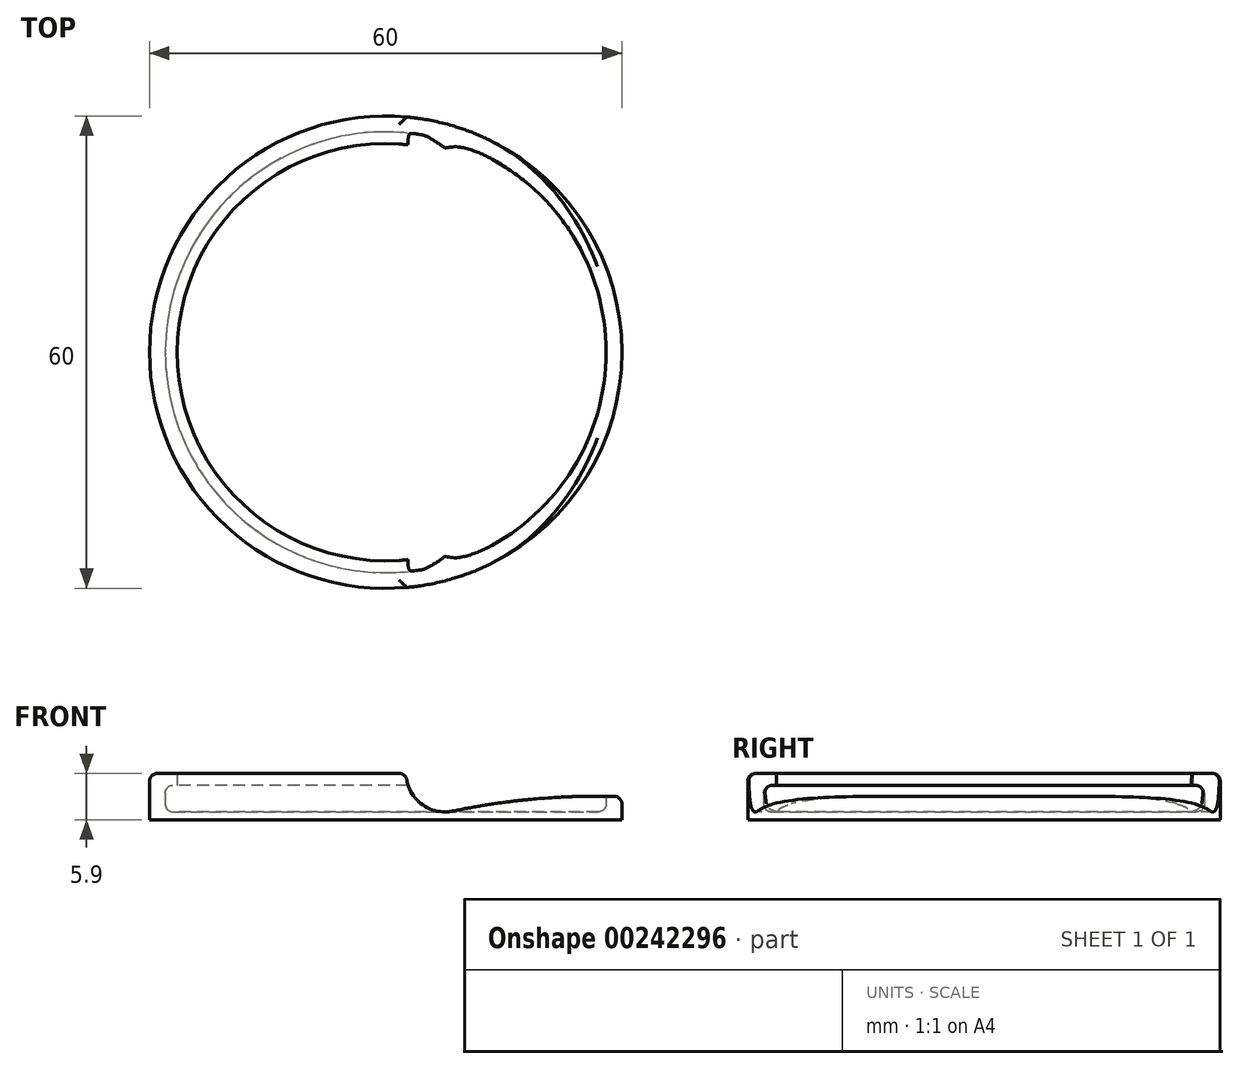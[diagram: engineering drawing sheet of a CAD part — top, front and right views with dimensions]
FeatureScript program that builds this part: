
annotation { "Feature Type Name" : "Feature", "Feature Type Description" : "" }
export const myFeature = defineFeature(function(context is Context, id is Id, definition is map)
    precondition{}
    {
        {
            var Q0;
            Q0=qCreatedBy(makeId("Front.planeOp"),FACE);
            var sketch = newSketch(context, id + "F0", { "sketchPlane" : qUnion([Q0])});
            skLineSegment(sketch, "E0", {"start": v(0, 0) * mm, "end": v(-27, 0) * mm});
            skLineSegment(sketch, "E1", {"start": v(-28, 1) * mm, "end": v(-28, 2.4) * mm});
            skLineSegment(sketch, "E2", {"start": v(-27, 3.4) * mm, "end": v(-26.5, 3.4) * mm});
            skLineSegment(sketch, "E3", {"start": v(-26.5, 3.4) * mm, "end": v(-26.5, 4.9) * mm});
            skLineSegment(sketch, "E4", {"start": v(-26.5, 4.9) * mm, "end": v(-29, 4.9) * mm});
            skLineSegment(sketch, "E5", {"start": v(-30, 3.9) * mm, "end": v(-30, -1) * mm});
            skLineSegment(sketch, "E6", {"start": v(0, -1) * mm, "end": v(0, 0) * mm});
            skPoint(sketch, "E7.visualSharp", {"position": v(-30, 4.9) * mm});
            skArc(sketch, "E7.filletArc", {"start": v(-29, 4.9) * mm, "mid": v(-29.7, 4.6) * mm, "end": v(-30, 3.9) * mm});
            skPoint(sketch, "E8.visualSharp", {"position": v(-28, 3.4) * mm});
            skArc(sketch, "E8.filletArc", {"start": v(-27, 3.4) * mm, "mid": v(-27.7, 3.1) * mm, "end": v(-28, 2.4) * mm});
            skPoint(sketch, "E9.visualSharp", {"position": v(-28, 0) * mm});
            skArc(sketch, "E9.filletArc", {"start": v(-28, 1) * mm, "mid": v(-27.7, 0.3) * mm, "end": v(-27, 0) * mm});
            skLineSegment(sketch, "E10", {"start": v(0, 0) * mm, "end": v(0, 0.5) * mm});
            skLineSegment(sketch, "E11", {"start": v(-28, 2) * mm, "end": v(-29, 2) * mm});
            skArc(sketch, "E12", {"start": v(-30, 1) * mm, "mid": v(-29.7, 1.7) * mm, "end": v(-29, 2) * mm});
            skLineSegment(sketch, "E13", {"start": v(0, -1) * mm, "end": v(-30, -1) * mm});
            skPoint(sketch, "E14.orphan", {"position": v(0, -2) * mm});
            skSolve(sketch);
        }
        {
            var Q0;
            Q0=makeQuery(id+"F0.imprint","IMPRINT",FACE,{"disambiguationData":[TD([[makeQuery(id+"F0.imprint","IMPRINT",EDGE,{"derivedFrom":sQuery(id+"F0.wireOp",EDGE,"E0")}),1.0]])]});
            var Q1;
            Q1=sQuery(id+"F0.wireOp",EDGE,"E6");
            revolve(context, id + "F1", {"entities" : qUnion([Q0]), "axis" : qUnion([Q1]), "revolveType" : RevolveType.FULL});
        }
        {
            var Q0;
            Q0=makeQuery(id+"F0.imprint","IMPRINT",FACE,{"disambiguationData":[TD([[makeQuery(id+"F0.imprint","IMPRINT",EDGE,{"derivedFrom":sQuery(id+"F0.wireOp",EDGE,"E2")}),1.0]])]});
            var Q1;
            Q1=sQuery(id+"F0.wireOp",EDGE,"E6");
            revolve(context, id + "F2", {"operationType" : NewBodyOperationType.ADD, "entities" : qUnion([Q0]), "axis" : qUnion([Q1]), "revolveType" : RevolveType.SYMMETRIC, "angle" : 210 * degree});
        }
        {
            var Q0;
            Q0=qCreatedBy(makeId("Front.planeOp"),FACE);
            var sketch = newSketch(context, id + "F3", { "sketchPlane" : qUnion([Q0])});
            skLineSegment(sketch, "E15.0", {"start": v(7.5, 4.9) * mm, "end": v(-29, 4.9) * mm});
            skLineSegment(sketch, "E16.0", {"start": v(7.5, 2) * mm, "end": v(29, 2) * mm});
            skCircle(sketch, "E17", {"center": v(7.5, 4.9) * mm, "radius": 4.9 * mm});
            skArc(sketch, "E18", {"start": v(2.68, 4.07) * mm, "mid": v(2.34, 4.66) * mm, "end": v(1.7, 4.9) * mm});
            skArc(sketch, "E19", {"start": v(26.89, 2) * mm, "mid": v(17.65, 1.52) * mm, "end": v(8.5, 0.1) * mm});
            skLineSegment(sketch, "E20.0.0", {"start": v(-27, 0) * mm, "end": v(27, 0) * mm});
            skSolve(sketch);
        }
        {
            var Q0;
            {var subQ0=sQuery(id+"F3.wireOp",EDGE,"E18");Q0=makeQuery(id+"F3.imprint","IMPRINT",FACE,{"disambiguationData":[TD([[makeQuery(id+"F3.imprint","IMPRINT",EDGE,{"derivedFrom":subQ0}),-1.0]])]});}
            var Q1;
            {var subQ0=sQuery(id+"F3.wireOp",EDGE,"E17");var subQ4=makeQuery(id+"F3.imprint","INTERSECT",VERTEX,{"derivedFrom":[subQ0,sQuery(id+"F3.wireOp",EDGE,"P1Wmpzot-LLGH-U3KA-p0y4-jWoeoiDEk2Na")]});Q1=makeQuery(id+"F3.imprint","IMPRINT",FACE,{"disambiguationData":[TD([[makeQuery(id+"F3.imprint","IMPRINT",EDGE,{"disambiguationData":[TD([[subQ4,1.0]])],"derivedFrom":subQ0}),1.0]])]});}
            var Q2;
            {var subQ0=sQuery(id+"F3.wireOp",EDGE,"E19");var subQ5=sQuery(id+"F3.wireOp",EDGE,"45842464-4a71-46be-bf13-90a27824be04.0");var subQ6=makeQuery(id+"F3.imprint","INTERSECT",VERTEX,{"derivedFrom":[subQ5,subQ0]});Q2=makeQuery(id+"F3.imprint","IMPRINT",FACE,{"disambiguationData":[TD([[makeQuery(id+"F3.imprint","IMPRINT",EDGE,{"disambiguationData":[TD([[subQ6,1.0]])],"derivedFrom":subQ5}),1.0]])]});}
            var Q3;
            {var subQ0=sQuery(id+"F3.wireOp",EDGE,"E19");Q3=makeQuery(id+"F3.imprint","IMPRINT",FACE,{"disambiguationData":[TD([[makeQuery(id+"F3.imprint","IMPRINT",EDGE,{"derivedFrom":subQ0}),-1.0]])]});}
            extrude(context, id + "F4", {"entities" : qUnion([Q0, Q1, Q2, Q3]), "operationType" : NewBodyOperationType.REMOVE, "oppositeDirection" : true, "depth" : 60 * mm, "symmetric" : true});
        }
    });
